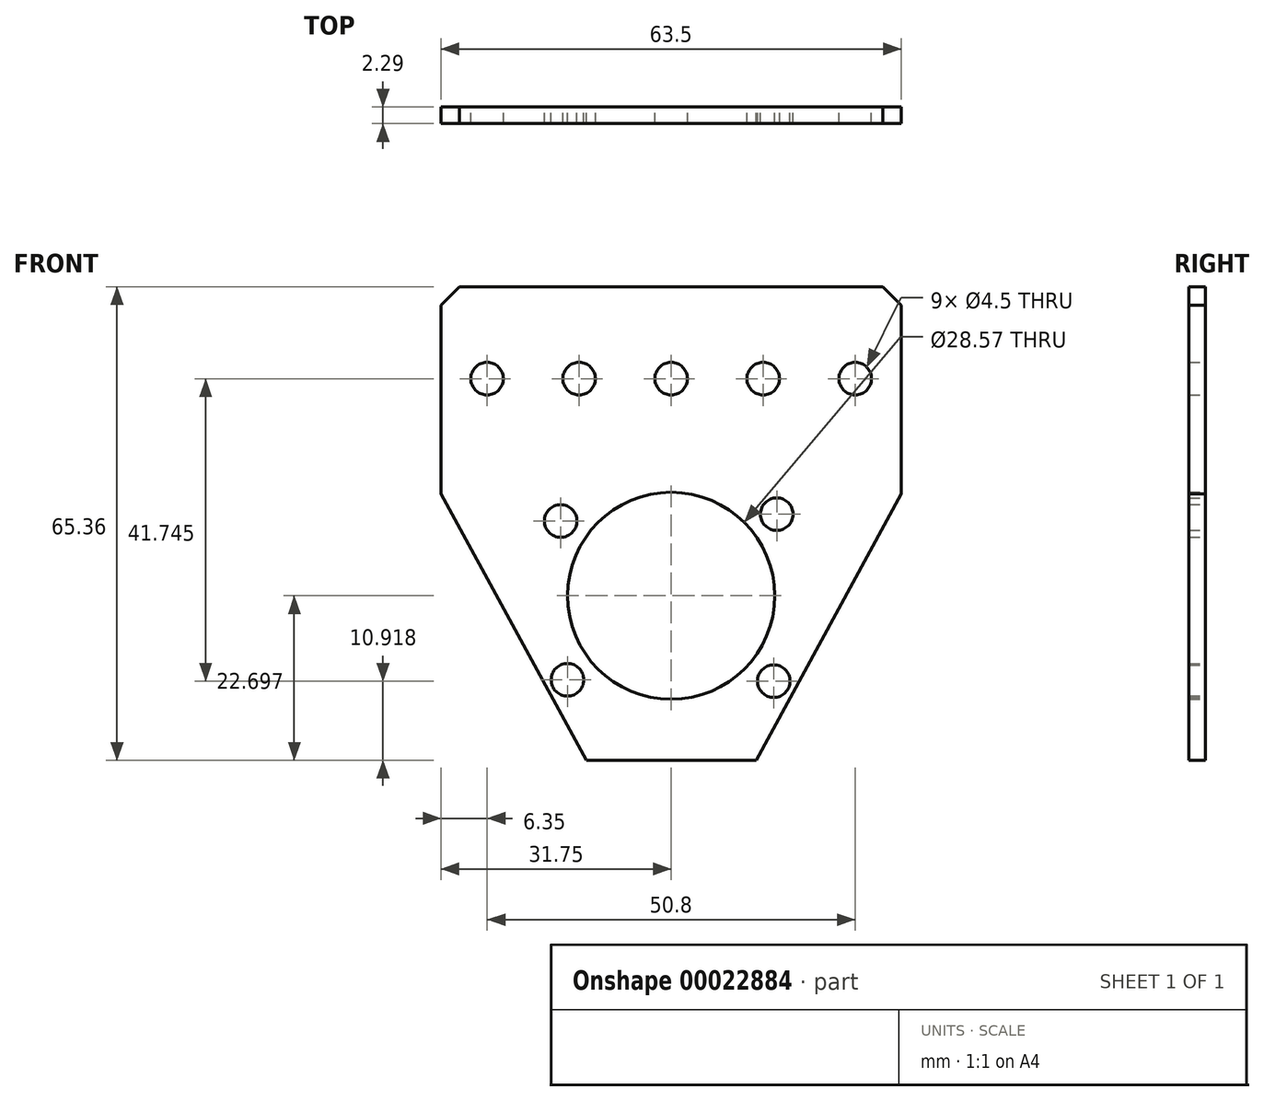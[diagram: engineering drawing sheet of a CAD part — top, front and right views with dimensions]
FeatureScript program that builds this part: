
annotation { "Feature Type Name" : "Feature", "Feature Type Description" : "" }
export const myFeature = defineFeature(function(context is Context, id is Id, definition is map)
    precondition{}
    {
        {
            var Q0;
            Q0=qCreatedBy(makeId("Front.planeOp"),FACE);
            var sketch = newSketch(context, id + "F0", { "sketchPlane" : qUnion([Q0])});
            skLineSegment(sketch, "E0.rect.bottom", {"start": v(31.75, 32.68) * mm, "end": v(-31.75, 32.68) * mm});
            skLineSegment(sketch, "E0.rect.top", {"start": v(11.7, -32.68) * mm, "end": v(-11.7, -32.68) * mm});
            skLineSegment(sketch, "E0.rect.left", {"start": v(31.75, 32.68) * mm, "end": v(31.75, 4.1) * mm});
            skLineSegment(sketch, "E0.rect.right", {"start": v(-31.75, 32.68) * mm, "end": v(-31.75, 4.1) * mm});
            skPoint(sketch, "E0.rect.middle", {"position": v(0, 0) * mm});
            skLineSegment(sketch, "E1", {"start": v(31.75, 4.1) * mm, "end": v(11.7, -32.68) * mm});
            skLineSegment(sketch, "E2", {"start": v(-31.75, 4.1) * mm, "end": v(-11.7, -32.68) * mm});
            skPoint(sketch, "E3.orphan", {"position": v(-29.51, 0) * mm});
            skPoint(sketch, "E4.orphan", {"position": v(29.51, 0) * mm});
            skPoint(sketch, "E5.orphan", {"position": v(-31.75, -32.68) * mm});
            skPoint(sketch, "E6.orphan", {"position": v(31.75, -32.68) * mm});
            skCircle(sketch, "E7", {"center": v(-12.7, 19.98) * mm, "radius": 2.25 * mm});
            skCircle(sketch, "E8", {"center": v(0, 19.98) * mm, "radius": 2.25 * mm});
            skCircle(sketch, "E9", {"center": v(12.7, 19.98) * mm, "radius": 2.25 * mm});
            skCircle(sketch, "E10", {"center": v(25.4, 19.98) * mm, "radius": 2.25 * mm});
            skCircle(sketch, "E11", {"center": v(-25.4, 19.98) * mm, "radius": 2.25 * mm});
            skCircle(sketch, "E12", {"center": v(0, -9.98) * mm, "radius": 18.41 * mm});
            skCircle(sketch, "E13", {"center": v(0, -9.98) * mm, "radius": 14.29 * mm});
            skCircle(sketch, "E14", {"center": v(-15.25, 0.34) * mm, "radius": 2.25 * mm});
            skCircle(sketch, "E15", {"center": v(14.57, 1.28) * mm, "radius": 2.25 * mm});
            skCircle(sketch, "E16", {"center": v(-14.3, -21.58) * mm, "radius": 2.25 * mm});
            skCircle(sketch, "E17", {"center": v(14.16, -21.76) * mm, "radius": 2.25 * mm});
            skSolve(sketch);
        }
        {
            var Q0;
            Q0=makeQuery(id+"F0.imprint","IMPRINT",FACE,{"disambiguationData":[TD([[makeQuery(id+"F0.imprint","IMPRINT",EDGE,{"derivedFrom":sQuery(id+"F0.wireOp",EDGE,"E0.rect.bottom")}),1.0]])]});
            var Q1;
            Q1=makeQuery(id+"F0.imprint","IMPRINT",FACE,{"disambiguationData":[TD([[makeQuery(id+"F0.imprint","IMPRINT",EDGE,{"derivedFrom":sQuery(id+"F0.wireOp",EDGE,"E13")}),-1.0]])]});
            extrude(context, id + "F1", {"entities" : qUnion([Q0, Q1]), "depth" : 2.3 * mm});
        }
        {
            var Q0;
            Q0=makeQuery(id+"F1.opExtrude","SWEPT_EDGE",EDGE,{"disambiguationData":[OSD([sQuery(id+"F0.wireOp",EDGE,"E0.rect.bottom"),sQuery(id+"F0.wireOp",EDGE,"E0.rect.left")])]});
            var Q1;
            Q1=makeQuery(id+"F1.opExtrude","SWEPT_EDGE",EDGE,{"disambiguationData":[OSD([sQuery(id+"F0.wireOp",EDGE,"E0.rect.bottom"),sQuery(id+"F0.wireOp",EDGE,"E0.rect.right")])]});
            chamfer(context, id + "F2", {"entities" : qUnion([Q0, Q1]), "width" : 2.54 * mm, "tangentPropagation" : true});
        }
    });
